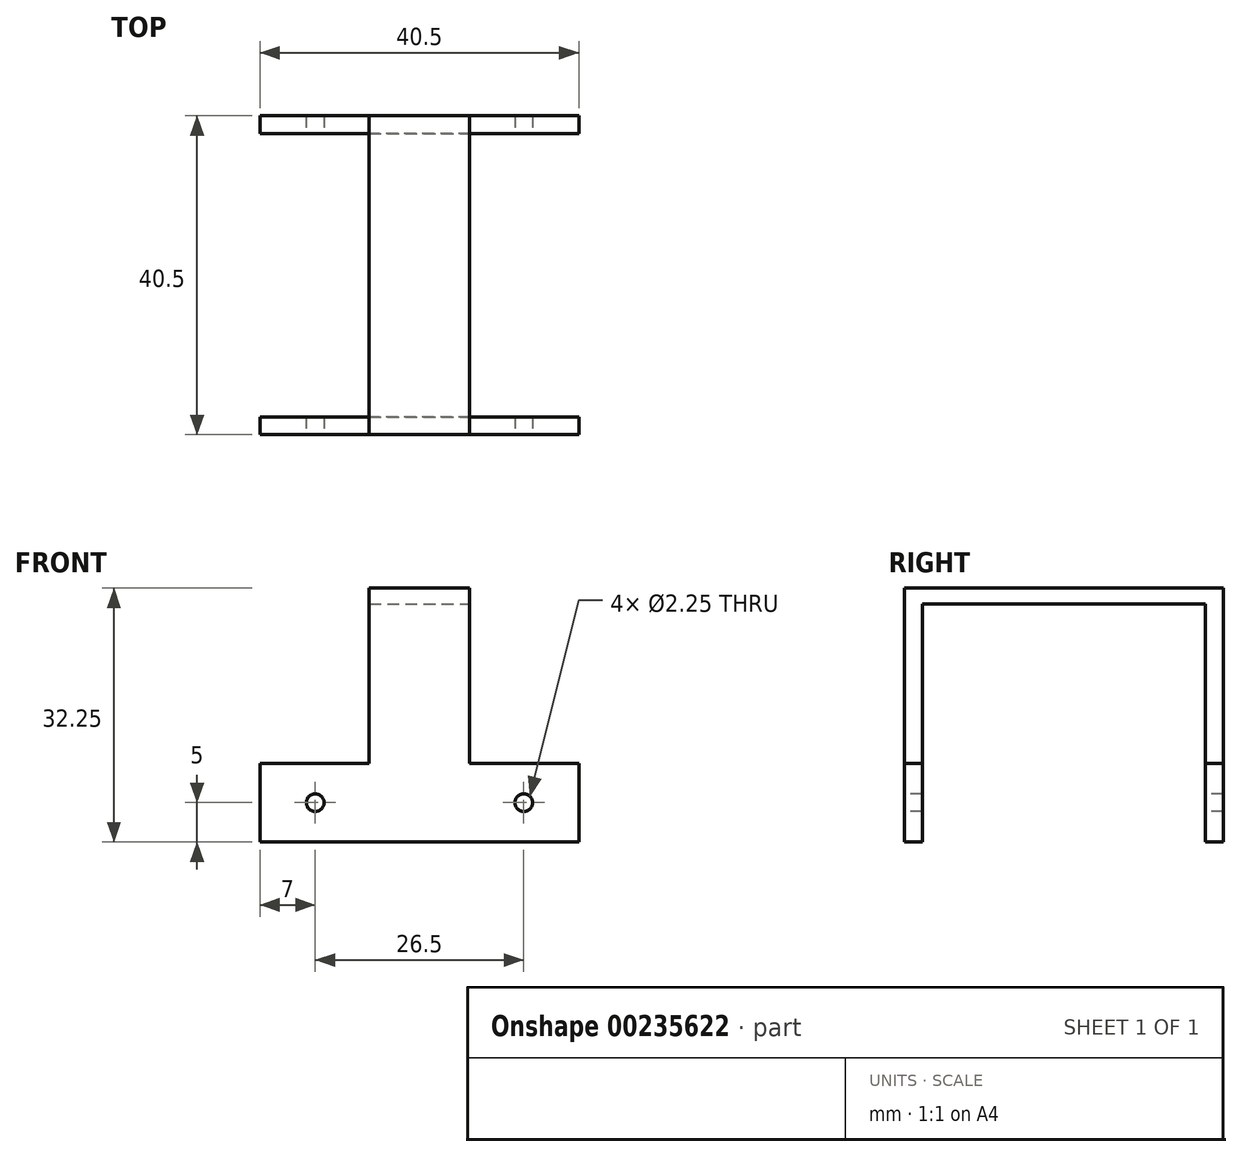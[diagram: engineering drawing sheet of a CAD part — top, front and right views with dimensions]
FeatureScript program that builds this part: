
annotation { "Feature Type Name" : "Feature", "Feature Type Description" : "" }
export const myFeature = defineFeature(function(context is Context, id is Id, definition is map)
    precondition{}
    {
        {
            var Q0;
            Q0=qCreatedBy(makeId("Top.planeOp"),FACE);
            var sketch = newSketch(context, id + "F0", { "sketchPlane" : qUnion([Q0])});
            skLineSegment(sketch, "E0.bottom", {"start": v(6.38, -20.25) * mm, "end": v(-6.38, -20.25) * mm});
            skLineSegment(sketch, "E0.top", {"start": v(6.38, 20.25) * mm, "end": v(-6.38, 20.25) * mm});
            skLineSegment(sketch, "E0.left", {"start": v(6.38, -20.25) * mm, "end": v(6.38, 20.25) * mm});
            skLineSegment(sketch, "E0.right", {"start": v(-6.38, -20.25) * mm, "end": v(-6.37, 20.25) * mm});
            skPoint(sketch, "E0.middle", {"position": v(0, 0) * mm});
            skSolve(sketch);
        }
        {
            var Q0;
            Q0=qCreatedBy(makeId("Front.planeOp"),FACE);
            var sketch = newSketch(context, id + "F1", { "sketchPlane" : qUnion([Q0])});
            skLineSegment(sketch, "E1.bottom", {"start": v(-6.38, 0) * mm, "end": v(6.38, 0) * mm});
            skLineSegment(sketch, "E1.top", {"start": v(-6.38, -20.25) * mm, "end": v(6.38, -20.25) * mm});
            skLineSegment(sketch, "E1.left", {"start": v(-6.38, 0) * mm, "end": v(-6.38, -20.25) * mm});
            skLineSegment(sketch, "E1.right", {"start": v(6.38, 0) * mm, "end": v(6.38, -20.25) * mm});
            skSolve(sketch);
        }
        {
            var Q0;
            Q0=makeQuery(id+"F0.imprint","IMPRINT",FACE,{"disambiguationData":[TD([[makeQuery(id+"F0.imprint","IMPRINT",EDGE,{"derivedFrom":sQuery(id+"F0.wireOp",EDGE,"E0.bottom")}),-1.0]])]});
            extrude(context, id + "F2", {"entities" : qUnion([Q0]), "depth" : 2 * mm});
        }
        {
            var Q0;
            Q0=makeQuery(id+"F1.imprint","IMPRINT",FACE,{"disambiguationData":[TD([[makeQuery(id+"F1.imprint","IMPRINT",EDGE,{"derivedFrom":sQuery(id+"F1.wireOp",EDGE,"E1.bottom")}),-1.0]])]});
            var Q1;
            Q1=makeQuery(id+"F2.opExtrude","SWEPT_FACE",FACE,{"disambiguationData":[OSD([sQuery(id+"F0.wireOp",EDGE,"E0.bottom")])]});
            extrude(context, id + "F3", {"entities" : qUnion([Q0]), "operationType" : NewBodyOperationType.ADD, "endBound" : BoundingType.UP_TO_SURFACE, "endBoundEntityFace" : qUnion([Q1]), "depth" : 11.94 * mm, "hasSecondDirection" : true, "secondDirectionOppositeDirection" : false, "secondDirectionDepth" : 18 * mm});
        }
        {
            var Q0;
            Q0=makeQuery(id+"F1.imprint","IMPRINT",FACE,{"disambiguationData":[TD([[makeQuery(id+"F1.imprint","IMPRINT",EDGE,{"derivedFrom":sQuery(id+"F1.wireOp",EDGE,"E1.bottom")}),-1.0]])]});
            var Q1;
            Q1=makeQuery(id+"F2.opExtrude","SWEPT_FACE",FACE,{"disambiguationData":[OSD([sQuery(id+"F0.wireOp",EDGE,"E0.top")])]});
            extrude(context, id + "F4", {"entities" : qUnion([Q0]), "operationType" : NewBodyOperationType.ADD, "endBound" : BoundingType.UP_TO_SURFACE, "oppositeDirection" : true, "endBoundEntityFace" : qUnion([Q1]), "depth" : 25.4 * mm, "hasSecondDirection" : true, "secondDirectionOppositeDirection" : true, "secondDirectionDepth" : 18 * mm});
        }
        {
            var Q0;
            Q0=makeQuery(id+"F4.boolean.opBoolean","MERGE",FACE,{"derivedFrom":[makeQuery(id+"F2.opExtrude","SWEPT_FACE",FACE,{"disambiguationData":[OSD([sQuery(id+"F0.wireOp",EDGE,"E0.top")])]}),makeQuery(id+"F4.opExtrude","CAP_FACE",FACE,{"disambiguationData":[OSD([sQuery(id+"F1.wireOp",EDGE,"E1.bottom"),sQuery(id+"F1.wireOp",EDGE,"E1.top"),sQuery(id+"F1.wireOp",EDGE,"E1.left"),sQuery(id+"F1.wireOp",EDGE,"E1.right")])],"isStart":false})]});
            var sketch = newSketch(context, id + "F5", { "sketchPlane" : qUnion([Q0])});
            skLineSegment(sketch, "E2", {"start": v(0, 2) * mm, "end": v(0, -20.25) * mm, "construction": true});
            skLineSegment(sketch, "E3.bottom", {"start": v(-20.25, -20.25) * mm, "end": v(20.25, -20.25) * mm});
            skLineSegment(sketch, "E3.top", {"start": v(-20.25, -30.25) * mm, "end": v(20.25, -30.25) * mm});
            skLineSegment(sketch, "E3.left", {"start": v(-20.25, -20.25) * mm, "end": v(-20.25, -30.25) * mm});
            skLineSegment(sketch, "E3.right", {"start": v(20.25, -20.25) * mm, "end": v(20.25, -30.25) * mm});
            skSolve(sketch);
        }
        {
            var Q0;
            Q0=makeQuery(id+"F5.imprint","IMPRINT",FACE,{"disambiguationData":[TD([[makeQuery(id+"F5.imprint","IMPRINT",EDGE,{"derivedFrom":sQuery(id+"F5.wireOp",EDGE,"E3.top")}),1.0]])]});
            var Q1;
            Q1=makeQuery(id+"F4.opExtrude","CAP_FACE",FACE,{"disambiguationData":[OSD([sQuery(id+"F1.wireOp",EDGE,"E1.bottom"),sQuery(id+"F1.wireOp",EDGE,"E1.top"),sQuery(id+"F1.wireOp",EDGE,"E1.left"),sQuery(id+"F1.wireOp",EDGE,"E1.right")])],"isStart":true});
            extrude(context, id + "F6", {"entities" : qUnion([Q0]), "operationType" : NewBodyOperationType.ADD, "endBound" : BoundingType.UP_TO_SURFACE, "oppositeDirection" : true, "endBoundEntityFace" : qUnion([Q1]), "depth" : 25.4 * mm});
        }
        {
            var Q0;
            Q0=makeQuery(id+"F3.boolean.opBoolean","MERGE",FACE,{"derivedFrom":[makeQuery(id+"F2.opExtrude","SWEPT_FACE",FACE,{"disambiguationData":[OSD([sQuery(id+"F0.wireOp",EDGE,"E0.bottom")])]}),makeQuery(id+"F3.opExtrude","CAP_FACE",FACE,{"disambiguationData":[OSD([sQuery(id+"F1.wireOp",EDGE,"E1.bottom"),sQuery(id+"F1.wireOp",EDGE,"E1.top"),sQuery(id+"F1.wireOp",EDGE,"E1.left"),sQuery(id+"F1.wireOp",EDGE,"E1.right")])],"isStart":false})]});
            var sketch = newSketch(context, id + "F7", { "sketchPlane" : qUnion([Q0])});
            skLineSegment(sketch, "E4.bottom", {"start": v(-20.25, -20.25) * mm, "end": v(20.25, -20.25) * mm});
            skLineSegment(sketch, "E4.top", {"start": v(-20.25, -30.25) * mm, "end": v(20.25, -30.25) * mm});
            skLineSegment(sketch, "E4.left", {"start": v(-20.25, -20.25) * mm, "end": v(-20.25, -30.25) * mm});
            skLineSegment(sketch, "E4.right", {"start": v(20.25, -20.25) * mm, "end": v(20.25, -30.25) * mm});
            skLineSegment(sketch, "E5", {"start": v(0, 2) * mm, "end": v(0, -20.25) * mm});
            skSolve(sketch);
        }
        {
            var Q0;
            Q0 = qSketchRegion(id + "F7", true);
            var Q1;
            Q1=makeQuery(id+"F3.opExtrude","CAP_FACE",FACE,{"disambiguationData":[OSD([sQuery(id+"F1.wireOp",EDGE,"E1.bottom"),sQuery(id+"F1.wireOp",EDGE,"E1.top"),sQuery(id+"F1.wireOp",EDGE,"E1.left"),sQuery(id+"F1.wireOp",EDGE,"E1.right")])],"isStart":true});
            extrude(context, id + "F8", {"entities" : qUnion([Q0]), "operationType" : NewBodyOperationType.ADD, "endBound" : BoundingType.UP_TO_SURFACE, "oppositeDirection" : true, "endBoundEntityFace" : qUnion([Q1]), "depth" : 25.4 * mm});
        }
        {
            var Q0;
            Q0=makeQuery(id+"F8.boolean.opBoolean","MERGE",FACE,{"derivedFrom":[makeQuery(id+"F3.boolean.opBoolean","MERGE",FACE,{"derivedFrom":[makeQuery(id+"F2.opExtrude","SWEPT_FACE",FACE,{"disambiguationData":[OSD([sQuery(id+"F0.wireOp",EDGE,"E0.bottom")])]}),makeQuery(id+"F3.opExtrude","CAP_FACE",FACE,{"disambiguationData":[OSD([sQuery(id+"F1.wireOp",EDGE,"E1.bottom"),sQuery(id+"F1.wireOp",EDGE,"E1.top"),sQuery(id+"F1.wireOp",EDGE,"E1.left"),sQuery(id+"F1.wireOp",EDGE,"E1.right")])],"isStart":false})]}),makeQuery(id+"F8.opExtrude","CAP_FACE",FACE,{"disambiguationData":[OSD([sQuery(id+"F7.wireOp",EDGE,"E4.bottom"),sQuery(id+"F7.wireOp",EDGE,"E4.top"),sQuery(id+"F7.wireOp",EDGE,"E4.left"),sQuery(id+"F7.wireOp",EDGE,"E4.right")])],"isStart":true})]});
            var sketch = newSketch(context, id + "F9", { "sketchPlane" : qUnion([Q0])});
            skLineSegment(sketch, "E6", {"start": v(-20.25, -25.25) * mm, "end": v(-13.25, -25.25) * mm, "construction": true});
            skLineSegment(sketch, "E7", {"start": v(20.25, -25.25) * mm, "end": v(13.25, -25.25) * mm, "construction": true});
            skCircle(sketch, "E8", {"center": v(-13.25, -25.25) * mm, "radius": 1.13 * mm});
            skCircle(sketch, "E9", {"center": v(13.25, -25.25) * mm, "radius": 1.13 * mm});
            skSolve(sketch);
        }
        {
            var Q0;
            Q0=makeQuery(id+"F9.imprint","IMPRINT",FACE,{"disambiguationData":[TD([[makeQuery(id+"F9.imprint","IMPRINT",EDGE,{"derivedFrom":sQuery(id+"F9.wireOp",EDGE,"E8")}),1.0]])]});
            var Q1;
            Q1=makeQuery(id+"F9.imprint","IMPRINT",FACE,{"disambiguationData":[TD([[makeQuery(id+"F9.imprint","IMPRINT",EDGE,{"derivedFrom":sQuery(id+"F9.wireOp",EDGE,"E9")}),1.0]])]});
            var Q2;
            Q2=sQuery(id+"F9.wireOp",EDGE,"E8");
            var Q3;
            Q3=sQuery(id+"F9.wireOp",EDGE,"E9");
            extrude(context, id + "F10", {"entities" : qUnion([Q0, Q1]), "operationType" : NewBodyOperationType.REMOVE, "surfaceEntities" : qUnion([Q2, Q3]), "endBound" : BoundingType.THROUGH_ALL, "oppositeDirection" : true, "depth" : 25.4 * mm});
        }
    });
